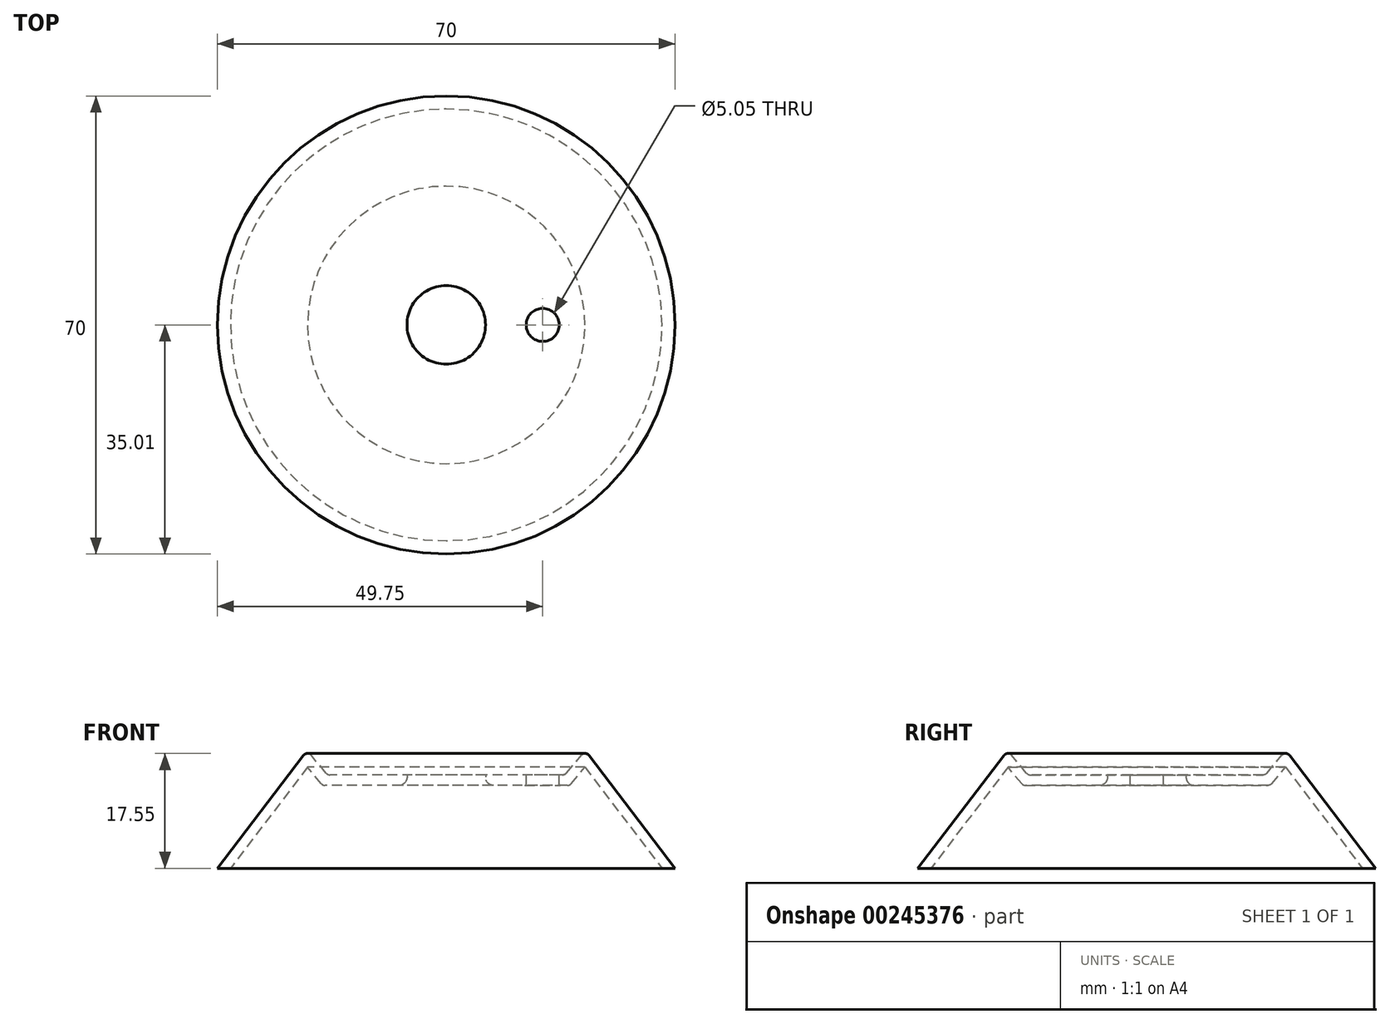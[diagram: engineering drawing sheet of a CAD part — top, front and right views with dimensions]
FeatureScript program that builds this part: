
annotation { "Feature Type Name" : "Feature", "Feature Type Description" : "" }
export const myFeature = defineFeature(function(context is Context, id is Id, definition is map)
    precondition{}
    {
        {
            var Q0;
            Q0=qCreatedBy(makeId("Front.planeOp"),FACE);
            var sketch = newSketch(context, id + "F0", { "sketchPlane" : qUnion([Q0])});
            skLineSegment(sketch, "E0", {"start": v(0, 0) * mm, "end": v(35, 0) * mm});
            skLineSegment(sketch, "E1", {"start": v(0, 0) * mm, "end": v(0, 18) * mm, "construction": true});
            skLineSegment(sketch, "E2", {"start": v(0, 18) * mm, "end": v(32.58, 18) * mm, "construction": true});
            skLineSegment(sketch, "E3", {"start": v(5.95, 0) * mm, "end": v(5.95, 14.28) * mm, "construction": true});
            skLineSegment(sketch, "E4", {"start": v(0, 14.28) * mm, "end": v(0, 0) * mm});
            skLineSegment(sketch, "E5", {"start": v(6.35, 0) * mm, "end": v(6.35, 13.76) * mm, "construction": true});
            skLineSegment(sketch, "E6", {"start": v(18.15, 0) * mm, "end": v(18.15, 18.32) * mm, "construction": true});
            skLineSegment(sketch, "E7", {"start": v(5.95, 14.28) * mm, "end": v(18.15, 14.28) * mm});
            skLineSegment(sketch, "E8", {"start": v(5.95, 14.28) * mm, "end": v(0, 14.28) * mm});
            skLineSegment(sketch, "E9", {"start": v(0, 14.28) * mm, "end": v(0, 14.28) * mm});
            skLineSegment(sketch, "E10", {"start": v(18.15, 14.28) * mm, "end": v(21.27, 18) * mm});
            skLineSegment(sketch, "E11", {"start": v(21.27, 18) * mm, "end": v(35, 0) * mm});
            skSolve(sketch);
        }
        {
            var Q0;
            Q0 = qSketchRegion(id + "F0", true);
            extrude(context, id + "F1", {"entities" : qUnion([Q0]), "depth" : 0.01 * mm});
        }
        {
            var Q0;
            Q0=makeQuery(id+"F1.opExtrude","CAP_FACE",FACE,{"disambiguationData":[OSD([sQuery(id+"F0.wireOp",EDGE,"E0"),sQuery(id+"F0.wireOp",EDGE,"6y4ub3ka-Ihgj-H0nH-vjQd-nl8F7qjLXdH2"),sQuery(id+"F0.wireOp",EDGE,"k02bPiOn-f1VR-HTtH-kJtN-WkPaZOF7wZD0"),sQuery(id+"F0.wireOp",EDGE,"ieqvGgUx-12EA-STK7-xuCT-3rcJsafOrvBf"),sQuery(id+"F0.wireOp",EDGE,"E4")])],"isStart":false});
            var Q1;
            Q1=makeQuery(id+"F1.opExtrude","CAP_EDGE",EDGE,{"disambiguationData":[OSD([sQuery(id+"F0.wireOp",EDGE,"E4")])],"isStart":false});
            revolve(context, id + "F2", {"operationType" : NewBodyOperationType.ADD, "entities" : qUnion([Q0]), "axis" : qUnion([Q1]), "revolveType" : RevolveType.FULL});
        }
        {
            var Q0;
            {var subQ0=sQuery(id+"F0.wireOp",EDGE,"E0");Q0=makeQuery(id+"F2.boolean.opBoolean","MERGE",FACE,{"derivedFrom":[makeQuery(id+"F1.opExtrude","SWEPT_FACE",FACE,{"disambiguationData":[OSD([subQ0])]}),makeQuery(id+"F2.opRevolve","SWEPT_FACE",FACE,{"disambiguationData":[OSD([subQ0])]})]});}
            shell(context, id + "F3", {"entities" : qUnion([Q0]), "thickness" : 1.6 * mm});
        }
        {
            var Q0;
            {var subQ0=sQuery(id+"F0.wireOp",EDGE,"E0");Q0=makeQuery(id+"F2.boolean.opBoolean","MERGE",FACE,{"derivedFrom":[makeQuery(id+"F1.opExtrude","SWEPT_FACE",FACE,{"disambiguationData":[OSD([subQ0])]}),makeQuery(id+"F2.opRevolve","SWEPT_FACE",FACE,{"disambiguationData":[OSD([subQ0])]})]});}
            var sketch = newSketch(context, id + "F4", { "sketchPlane" : qUnion([Q0])});
            skCircle(sketch, "E12", {"center": v(0, 0.01) * mm, "radius": 6 * mm});
            skCircle(sketch, "E13", {"center": v(0, 0) * mm, "radius": 6 * mm});
            skSolve(sketch);
        }
        {
            var Q0;
            Q0 = qSketchRegion(id + "F4", true);
            extrude(context, id + "F5", {"entities" : qUnion([Q0]), "operationType" : NewBodyOperationType.REMOVE, "oppositeDirection" : true, "depth" : 25 * mm});
        }
        {
            var Q0;
            Q0=makeQuery(id+"F2.opRevolve","SWEPT_EDGE",EDGE,{"disambiguationData":[OSD([sQuery(id+"F0.wireOp",EDGE,"i9SMpdhX-wvvY-t68j-uvlp-M6atMLKetHad"),sQuery(id+"F0.wireOp",EDGE,"nQEzmBRy-utbv-yRns-fLHs-DP6wbvmXK7bY")])]});
            var Q1;
            Q1=makeQuery(id+"F2.opRevolve","SWEPT_EDGE",EDGE,{"disambiguationData":[OSD([sQuery(id+"F0.wireOp",EDGE,"E7"),sQuery(id+"F0.wireOp",EDGE,"nQEzmBRy-utbv-yRns-fLHs-DP6wbvmXK7bY")])]});
            var Q2;
            {var subQ0=sQuery(id+"F0.wireOp",EDGE,"nQEzmBRy-utbv-yRns-fLHs-DP6wbvmXK7bY");var subQ1=sQuery(id+"F0.wireOp",EDGE,"E7");Q2=makeQuery(id+"F3.opShell","OFFSET_EDGE",EDGE,{"disambiguationData":[OSD([subQ1,subQ0]),TDD([makeQuery(id+"F2.opRevolve","SWEPT_EDGE",EDGE,{"disambiguationData":[OSD([subQ1,subQ0])]})])]});}
            var Q3;
            {var subQ0=sQuery(id+"F0.wireOp",EDGE,"nQEzmBRy-utbv-yRns-fLHs-DP6wbvmXK7bY");var subQ1=sQuery(id+"F0.wireOp",EDGE,"i9SMpdhX-wvvY-t68j-uvlp-M6atMLKetHad");Q3=makeQuery(id+"F3.opShell","OFFSET_EDGE",EDGE,{"disambiguationData":[OSD([subQ1,subQ0]),TDD([makeQuery(id+"F2.opRevolve","SWEPT_EDGE",EDGE,{"disambiguationData":[OSD([subQ1,subQ0])]})])]});}
            var Q4;
            Q4=makeQuery(id+"F2.opRevolve","SWEPT_EDGE",EDGE,{"disambiguationData":[OSD([sQuery(id+"F0.wireOp",EDGE,"E10"),sQuery(id+"F0.wireOp",EDGE,"E11")])]});
            fillet(context, id + "F6", {"entities" : qUnion([Q0, Q1, Q2, Q3, Q4]), "radius" : 0.75 * mm, "tangentPropagation" : true, "allowEdgeOverflow" : false});
        }
        {
            var Q0;
            Q0=makeQuery(id+"F5.boolean.opBoolean","INTERSECT",EDGE,{"derivedFrom":[makeQuery(id+"F3.opShell","OFFSET_FACE",FACE,{"disambiguationData":[OSD([sQuery(id+"F0.wireOp",EDGE,"E7"),sQuery(id+"F0.wireOp",EDGE,"E8")])]}),makeQuery(id+"F5.opExtrude","SWEPT_FACE",FACE,{"disambiguationData":[OSD([sQuery(id+"F4.wireOp",EDGE,"E12")])]})]});
            var Q1;
            Q1=makeQuery(id+"F5.boolean.opBoolean","INTERSECT",EDGE,{"derivedFrom":[makeQuery(id+"F3.opShell","OFFSET_FACE",FACE,{"disambiguationData":[OSD([sQuery(id+"F0.wireOp",EDGE,"E7"),sQuery(id+"F0.wireOp",EDGE,"E8")])]}),makeQuery(id+"F5.opExtrude","SWEPT_FACE",FACE,{"disambiguationData":[OSD([sQuery(id+"F4.wireOp",EDGE,"E13")])]})]});
            fillet(context, id + "F7", {"entities" : qUnion([Q0, Q1]), "radius" : 1.25 * mm, "tangentPropagation" : true, "allowEdgeOverflow" : false});
        }
        {
            var Q0;
            {var subQ0=sQuery(id+"F0.wireOp",EDGE,"E8");var subQ1=sQuery(id+"F0.wireOp",EDGE,"E7");Q0=makeQuery(id+"F2.boolean.opBoolean","MERGE",FACE,{"derivedFrom":[makeQuery(id+"F1.opExtrude","SWEPT_FACE",FACE,{"disambiguationData":[OSD([subQ1,subQ0])]}),makeQuery(id+"F2.opRevolve","SWEPT_FACE",FACE,{"disambiguationData":[OSD([subQ1,subQ0])]})]});}
            var sketch = newSketch(context, id + "F8", { "sketchPlane" : qUnion([Q0])});
            skLineSegment(sketch, "E14", {"start": v(0, 0) * mm, "end": v(14.75, 0) * mm, "construction": true});
            skCircle(sketch, "E15", {"center": v(14.75, 0) * mm, "radius": 2.52 * mm});
            skSolve(sketch);
        }
        {
            var Q0;
            Q0=makeQuery(id+"F8.imprint","IMPRINT",FACE,{"disambiguationData":[TD([[makeQuery(id+"F8.imprint","IMPRINT",EDGE,{"derivedFrom":sQuery(id+"F8.wireOp",EDGE,"E15")}),1.0]])]});
            var Q1;
            Q1 = qConstructionFilter(qBodyType(qCreatedBy(id + "F8" ,EDGE), BodyType.WIRE), ConstructionObject.NO);
            extrude(context, id + "F9", {"entities" : qUnion([Q0]), "operationType" : NewBodyOperationType.REMOVE, "surfaceEntities" : qUnion([Q1]), "oppositeDirection" : true, "depth" : 25 * mm});
        }
        {
            var Q0;
            Q0=makeQuery(id+"F9.boolean.opBoolean","COPY",EDGE,{"derivedFrom":makeQuery(id+"F9.opExtrude","CAP_EDGE",EDGE,{"disambiguationData":[OSD([sQuery(id+"F8.wireOp",EDGE,"E15")])],"isStart":true})});
            var Q1;
            Q1=makeQuery(id+"F9.boolean.opBoolean","INTERSECT",EDGE,{"derivedFrom":[makeQuery(id+"F3.opShell","OFFSET_FACE",FACE,{"disambiguationData":[OSD([sQuery(id+"F0.wireOp",EDGE,"E7"),sQuery(id+"F0.wireOp",EDGE,"E8")])]}),makeQuery(id+"F9.opExtrude","SWEPT_FACE",FACE,{"disambiguationData":[OSD([sQuery(id+"F8.wireOp",EDGE,"E15")])]})]});
            fillet(context, id + "F10", {"entities" : qUnion([Q0, Q1]), "radius" : 0.2 * mm, "tangentPropagation" : true, "allowEdgeOverflow" : false});
        }
    });
